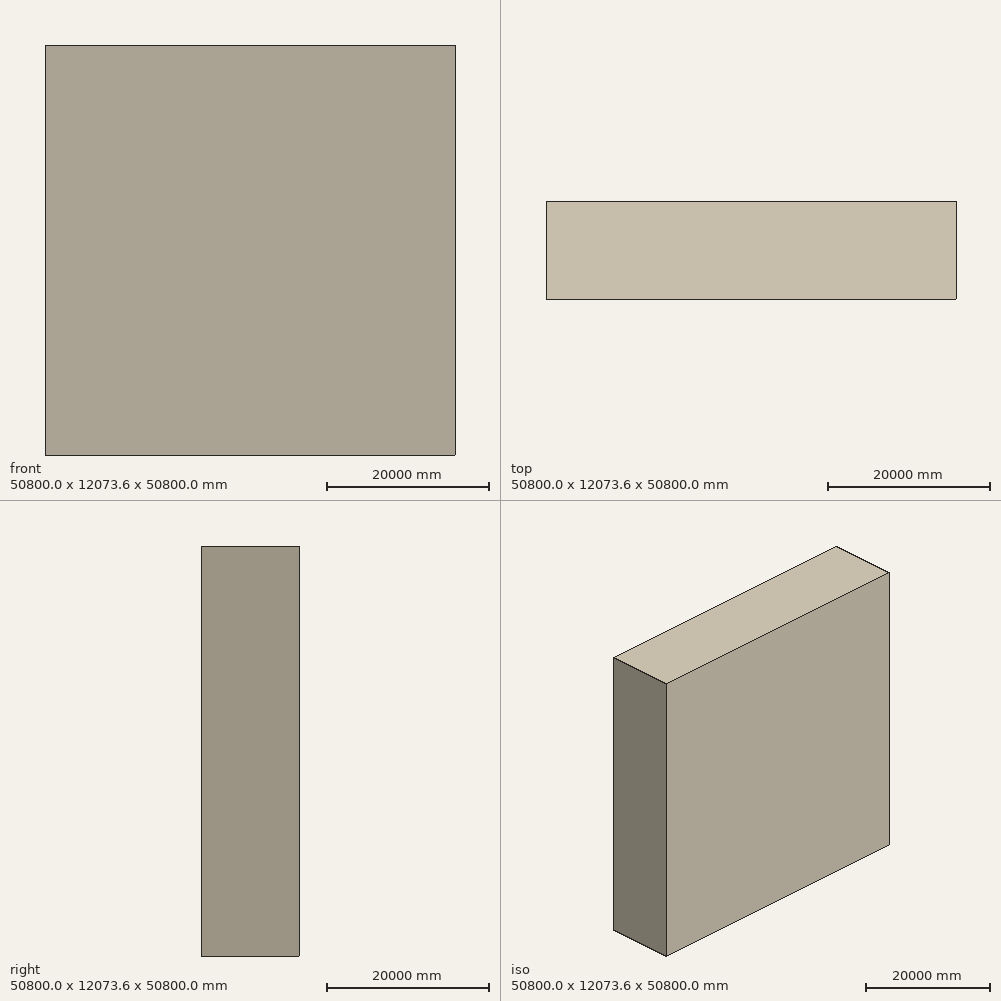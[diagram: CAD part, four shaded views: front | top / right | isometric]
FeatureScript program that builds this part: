
annotation { "Feature Type Name" : "Feature", "Feature Type Description" : "" }
export const myFeature = defineFeature(function(context is Context, id is Id, definition is map)
    precondition{}
    {
        {
            var Q0;
            Q0=qCreatedBy(makeId("Front.planeOp"),FACE);
            var sketch = newSketch(context, id + "F0", { "sketchPlane" : qUnion([Q0])});
            skLineSegment(sketch, "E0.bottom", {"start": v(0, 0) * mm, "end": v(50800, 0) * mm});
            skLineSegment(sketch, "E0.top", {"start": v(0, 50800) * mm, "end": v(50800, 50800) * mm});
            skLineSegment(sketch, "E0.left", {"start": v(0, 0) * mm, "end": v(0, 50800) * mm});
            skLineSegment(sketch, "E0.right", {"start": v(50800, 0) * mm, "end": v(50800, 50800) * mm});
            skSolve(sketch);
        }
        {
            var Q0;
            Q0 = qSketchRegion(id + "F0", true);
            extrude(context, id + "F1", {"entities" : qUnion([Q0]), "depth" : 12073.6 * mm});
        }
    });
